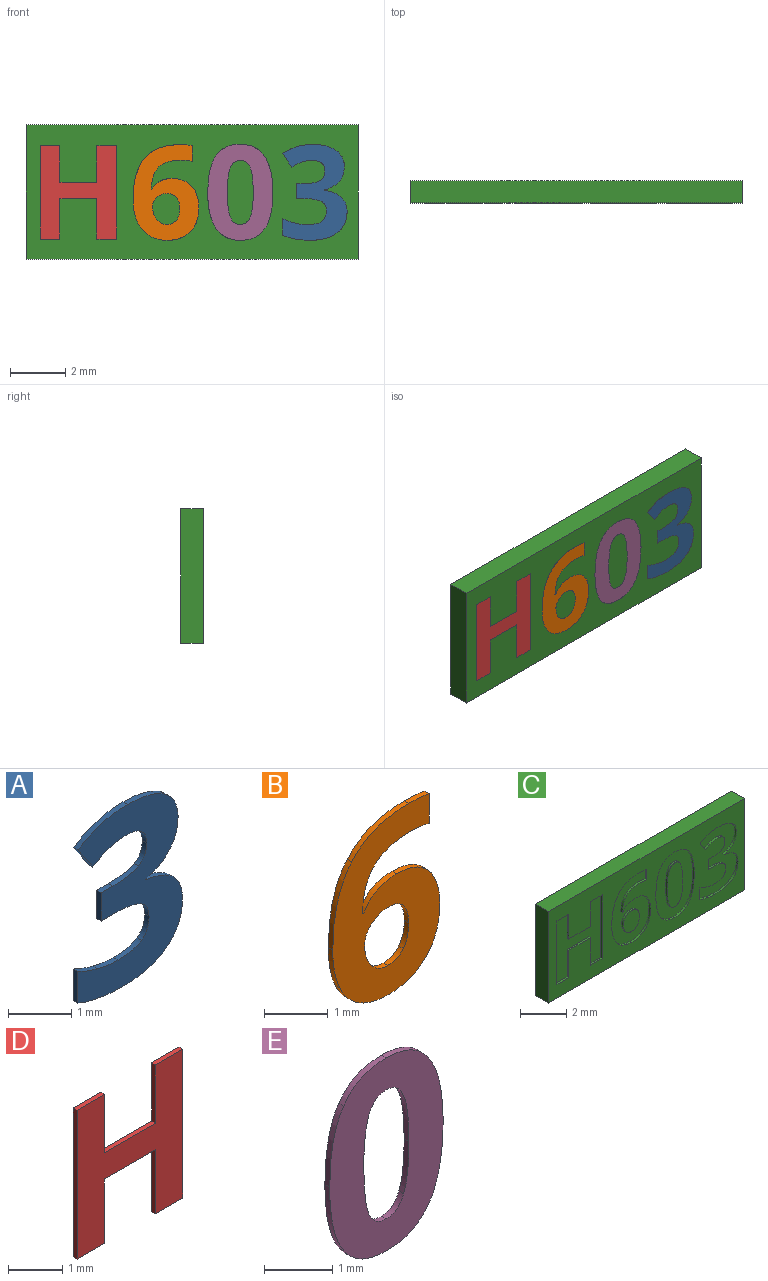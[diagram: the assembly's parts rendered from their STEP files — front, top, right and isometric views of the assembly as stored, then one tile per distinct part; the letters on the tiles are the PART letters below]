
ASSEMBLY  parts=5 mates=4
PART A: 29 faces, bbox 2.3x0.1x3.5 mm
  f0: plane 3.47x2.33mm, normal (0,-1,0), area 4.3mm2, adj f1,f2,f3,f4,f5,f6,f7,f8
  f1: extruded ~0.83x0.21mm, area 0.1mm2, adj f0,f2,f25,f27
  f2: extruded ~1.1x0.33mm, area 0.1mm2, adj f0,f1,f3,f25
  f3: plane 0.49x0.33mm, normal (-0.83,0,-0.56), area 0.1mm2, adj f0,f2,f4,f25
  f4: extruded ~0.38x0.19mm, area 0mm2, adj f0,f3,f5,f25
  f5: extruded ~0.34x0.1mm, area 0mm2, adj f0,f4,f6,f25
  f6: extruded ~0.48x0.38mm, area 0.1mm2, adj f0,f5,f7,f25
  f7: extruded ~0.35x0.18mm, area 0mm2, adj f0,f6,f8,f25
  f8: extruded ~0.57x0.1mm, area 0.1mm2, adj f0,f7,f9,f25
  f9: plane 0.26x0.1mm, normal (0,0,1), area 0mm2, adj f0,f8,f10,f25
  f10: plane 0.55x0.1mm, normal (-1,0,0), area 0.1mm2, adj f0,f9,f11,f25
  f11: plane 0.26x0.1mm, normal (0,0,-1), area 0mm2, adj f0,f10,f12,f25
  f12: extruded ~0.62x0.1mm, area 0.1mm2, adj f0,f11,f13,f25
  f13: extruded ~0.34x0.19mm, area 0mm2, adj f0,f12,f14,f25
  f14: extruded ~0.39x0.17mm, area 0mm2, adj f0,f13,f15,f25
  f15: extruded ~0.52x0.12mm, area 0.1mm2, adj f0,f14,f16,f25
  f16: extruded ~0.47x0.1mm, area 0mm2, adj f0,f15,f17,f25
  f17: extruded ~0.43x0.16mm, area 0mm2, adj f0,f16,f18,f25
  f18: plane 0.61x0.1mm, normal (-1,0,0), area 0.1mm2, adj f0,f17,f19,f25
  f19: extruded ~0.97x0.18mm, area 0.1mm2, adj f0,f18,f20,f25
  f20: extruded ~1.01x0.27mm, area 0.1mm2, adj f0,f19,f21,f25
  f21: extruded ~0.76x0.35mm, area 0.1mm2, adj f0,f20,f22,f25
  f22: extruded ~0.53x0.21mm, area 0.1mm2, adj f0,f21,f23,f25
  f23: extruded ~0.62x0.25mm, area 0.1mm2, adj f0,f22,f24,f25
  f24: plane 0.1x0.01mm, normal (1,0,0), area 0mm2, adj f0,f23,f25,f26
  f25: plane 3.47x2.33mm, normal (0,1,0), area 4.3mm2, adj f1,f2,f3,f4,f5,f6,f7,f8
  f26: extruded ~0.54x0.3mm, area 0.1mm2, adj f0,f24,f25,f28
  f27: extruded ~0.59x0.3mm, area 0.1mm2, adj f0,f1,f25,f28
  f28: extruded ~0.54x0.19mm, area 0.1mm2, adj f0,f25,f26,f27
PART B: 27 faces, bbox 2.4x0.1x3.5 mm
  f0: plane 3.46x2.38mm, normal (0,-1,0), area 4.8mm2, adj f1,f2,f3,f4,f5,f6,f7,f8
  f1: extruded ~0.51x0.43mm, area 0.1mm2, adj f0,f2,f20,f22
  f2: extruded ~0.65x0.17mm, area 0.1mm2, adj f0,f1,f3,f20
  f3: extruded ~0.84x0.32mm, area 0.1mm2, adj f0,f2,f4,f20
  f4: extruded ~0.85x0.3mm, area 0.1mm2, adj f0,f3,f5,f20
  f5: extruded ~0.78x0.26mm, area 0.1mm2, adj f0,f4,f6,f20
  f6: extruded ~0.71x0.28mm, area 0.1mm2, adj f0,f5,f7,f20
  f7: extruded ~0.73x0.39mm, area 0.1mm2, adj f0,f6,f8,f20
  f8: plane 0.1x0.03mm, normal (0,0,1), area 0mm2, adj f0,f7,f9,f20
  f9: extruded ~0.62x0.14mm, area 0.1mm2, adj f0,f8,f10,f20
  f10: extruded ~0.35x0.33mm, area 0mm2, adj f0,f9,f11,f20
  f11: extruded ~0.6x0.11mm, area 0.1mm2, adj f0,f10,f12,f20
  f12: extruded ~0.41x0.1mm, area 0mm2, adj f0,f11,f13,f20
  f13: plane 0.57x0.1mm, normal (1,0,0), area 0.1mm2, adj f0,f12,f14,f20
  f14: extruded ~0.45x0.1mm, area 0mm2, adj f0,f13,f20,f21
  f15: extruded ~0.46x0.14mm, area 0mm2, adj f0,f16,f20,f25
  f16: extruded ~0.33x0.15mm, area 0mm2, adj f0,f15,f17,f20
  f17: extruded ~0.37x0.14mm, area 0mm2, adj f0,f16,f18,f20
  f18: extruded ~0.34x0.14mm, area 0mm2, adj f0,f17,f19,f20
  f19: extruded ~0.39x0.11mm, area 0mm2, adj f0,f18,f20,f24
  f20: plane 3.46x2.38mm, normal (0,1,0), area 4.8mm2, adj f1,f2,f3,f4,f5,f6,f7,f8
  f21: extruded ~1.27x0.49mm, area 0.1mm2, adj f0,f14,f20,f23
  f22: extruded ~0.8x0.15mm, area 0.1mm2, adj f0,f1,f20,f23
  f23: extruded ~1.49x0.42mm, area 0.2mm2, adj f0,f20,f21,f22
  f24: extruded ~0.44x0.12mm, area 0mm2, adj f0,f19,f20,f26
  f25: extruded ~0.37x0.19mm, area 0mm2, adj f0,f15,f20,f26
  f26: extruded ~0.35x0.15mm, area 0mm2, adj f0,f20,f24,f25
PART C: 92 faces, bbox 12x0.8x4.9 mm
  f0: plane 12x4.85mm, normal (0,-1,0), area 35.7mm2, adj f1,f2,f3,f4,f6,f7,f8,f9
  f1: plane 12x0.8mm, normal (0,0,-1), area 9.6mm2, adj f0,f2,f4,f5
  f2: plane 4.85x0.8mm, normal (1,0,0), area 3.9mm2, adj f0,f1,f3,f5
  f3: plane 12x0.8mm, normal (0,0,1), area 9.6mm2, adj f0,f2,f4,f5
  f4: plane 4.85x0.8mm, normal (-1,0,0), area 3.9mm2, adj f0,f1,f3,f5
  f5: plane 12x4.85mm, normal (0,1,0), area 58.2mm2, adj f1,f2,f3,f4
  f6: extruded ~0.59x0.3mm, area 0.1mm2, adj f0,f7,f32,f33
  f7: extruded ~0.83x0.21mm, area 0.1mm2, adj f0,f6,f8,f33
  f8: extruded ~1.1x0.33mm, area 0.1mm2, adj f0,f7,f9,f33
  f9: plane 0.49x0.33mm, normal (0.83,0,0.56), area 0.1mm2, adj f0,f8,f10,f33
  f10: extruded ~0.38x0.19mm, area 0mm2, adj f0,f9,f11,f33
  f11: extruded ~0.34x0.1mm, area 0mm2, adj f0,f10,f12,f33
  f12: extruded ~0.48x0.38mm, area 0.1mm2, adj f0,f11,f13,f33
  f13: extruded ~0.35x0.18mm, area 0mm2, adj f0,f12,f14,f33
  f14: extruded ~0.57x0.1mm, area 0.1mm2, adj f0,f13,f15,f33
  f15: plane 0.26x0.1mm, normal (0,0,-1), area 0mm2, adj f0,f14,f16,f33
  f16: plane 0.55x0.1mm, normal (1,0,0), area 0.1mm2, adj f0,f15,f17,f33
  f17: plane 0.26x0.1mm, normal (0,0,1), area 0mm2, adj f0,f16,f18,f33
  f18: extruded ~0.62x0.1mm, area 0.1mm2, adj f0,f17,f19,f33
  f19: extruded ~0.34x0.19mm, area 0mm2, adj f0,f18,f20,f33
  f20: extruded ~0.39x0.17mm, area 0mm2, adj f0,f19,f21,f33
  f21: extruded ~0.52x0.12mm, area 0.1mm2, adj f0,f20,f22,f33
  f22: extruded ~0.47x0.1mm, area 0mm2, adj f0,f21,f23,f33
  f23: extruded ~0.43x0.16mm, area 0mm2, adj f0,f22,f24,f33
  f24: plane 0.61x0.1mm, normal (1,0,0), area 0.1mm2, adj f0,f23,f25,f33
  f25: extruded ~0.97x0.18mm, area 0.1mm2, adj f0,f24,f26,f33
  f26: extruded ~1.01x0.27mm, area 0.1mm2, adj f0,f25,f27,f33
  f27: extruded ~0.76x0.35mm, area 0.1mm2, adj f0,f26,f28,f33
  f28: extruded ~0.53x0.21mm, area 0.1mm2, adj f0,f27,f29,f33
  f29: extruded ~0.62x0.25mm, area 0.1mm2, adj f0,f28,f30,f33
  f30: plane 0.1x0.01mm, normal (-1,0,0), area 0mm2, adj f0,f29,f31,f33
  f31: extruded ~0.54x0.3mm, area 0.1mm2, adj f0,f30,f32,f33
  f32: extruded ~0.54x0.19mm, area 0.1mm2, adj f0,f6,f31,f33
  f33: plane 3.47x2.33mm, normal (0,-1,0), area 4.3mm2, adj f6,f7,f8,f9,f10,f11,f12,f13
  f34: extruded ~0.8x0.15mm, area 0.1mm2, adj f0,f35,f58,f59
  f35: extruded ~0.51x0.43mm, area 0.1mm2, adj f0,f34,f36,f59
  f36: extruded ~0.65x0.17mm, area 0.1mm2, adj f0,f35,f37,f59
  f37: extruded ~0.84x0.32mm, area 0.1mm2, adj f0,f36,f38,f59
  f38: extruded ~0.85x0.3mm, area 0.1mm2, adj f0,f37,f39,f59
  f39: extruded ~0.78x0.26mm, area 0.1mm2, adj f0,f38,f40,f59
  f40: extruded ~0.71x0.28mm, area 0.1mm2, adj f0,f39,f41,f59
  f41: extruded ~0.73x0.39mm, area 0.1mm2, adj f0,f40,f42,f59
  f42: plane 0.1x0.03mm, normal (0,0,-1), area 0mm2, adj f0,f41,f43,f59
  f43: extruded ~0.62x0.14mm, area 0.1mm2, adj f0,f42,f44,f59
  f44: extruded ~0.35x0.33mm, area 0mm2, adj f0,f43,f45,f59
  f45: extruded ~0.6x0.11mm, area 0.1mm2, adj f0,f44,f46,f59
  f46: extruded ~0.41x0.1mm, area 0mm2, adj f0,f45,f47,f59
  f47: plane 0.57x0.1mm, normal (-1,0,0), area 0.1mm2, adj f0,f46,f48,f59
  f48: extruded ~0.45x0.1mm, area 0mm2, adj f0,f47,f49,f59
  f49: extruded ~1.27x0.49mm, area 0.1mm2, adj f0,f48,f58,f59
  f50: extruded ~0.37x0.19mm, area 0mm2, adj f51,f57,f59,f60
  f51: extruded ~0.46x0.14mm, area 0mm2, adj f50,f52,f59,f60
  f52: extruded ~0.33x0.15mm, area 0mm2, adj f51,f53,f59,f60
  f53: extruded ~0.37x0.14mm, area 0mm2, adj f52,f54,f59,f60
  f54: extruded ~0.34x0.14mm, area 0mm2, adj f53,f55,f59,f60
  f55: extruded ~0.39x0.11mm, area 0mm2, adj f54,f56,f59,f60
  f56: extruded ~0.44x0.12mm, area 0mm2, adj f55,f57,f59,f60
  f57: extruded ~0.35x0.15mm, area 0mm2, adj f50,f56,f59,f60
  f58: extruded ~1.49x0.42mm, area 0.2mm2, adj f0,f34,f49,f59
  f59: plane 3.46x2.38mm, normal (0,-1,0), area 4.8mm2, adj f34,f35,f36,f37,f38,f39,f40,f41
  f60: plane 1.12x0.98mm, normal (0,-1,0), area 0.9mm2, adj f50,f51,f52,f53,f54,f55,f56,f57
  f61: extruded ~1.3x0.3mm, area 0.1mm2, adj f0,f62,f76,f77
  f62: extruded ~0.88x0.44mm, area 0.1mm2, adj f0,f61,f63,f77
  f63: extruded ~0.89x0.42mm, area 0.1mm2, adj f0,f62,f64,f77
  f64: extruded ~1.32x0.29mm, area 0.1mm2, adj f0,f63,f65,f77
  f65: extruded ~1.29x0.3mm, area 0.1mm2, adj f0,f64,f66,f77
  f66: extruded ~0.88x0.44mm, area 0.1mm2, adj f0,f65,f67,f77
  f67: extruded ~0.89x0.42mm, area 0.1mm2, adj f0,f66,f76,f77
  f68: extruded ~0.89x0.11mm, area 0.1mm2, adj f69,f75,f77,f78
  f69: extruded ~0.36x0.27mm, area 0mm2, adj f68,f70,f77,f78
  f70: extruded ~0.36x0.27mm, area 0mm2, adj f69,f71,f77,f78
  f71: extruded ~0.89x0.11mm, area 0.1mm2, adj f70,f72,f77,f78
  f72: extruded ~0.89x0.11mm, area 0.1mm2, adj f71,f73,f77,f78
  f73: extruded ~0.36x0.27mm, area 0mm2, adj f72,f74,f77,f78
  f74: extruded ~0.36x0.27mm, area 0mm2, adj f73,f75,f77,f78
  f75: extruded ~0.89x0.11mm, area 0.1mm2, adj f68,f74,f77,f78
  f76: extruded ~1.31x0.29mm, area 0.1mm2, adj f0,f61,f67,f77
  f77: plane 3.47x2.36mm, normal (0,-1,0), area 5mm2, adj f61,f62,f63,f64,f65,f66,f67,f68
  f78: plane 2.32x0.94mm, normal (0,-1,0), area 1.8mm2, adj f68,f69,f70,f71,f72,f73,f74,f75
  f79: plane 3.37x0.1mm, normal (-1,0,0), area 0.3mm2, adj f0,f80,f90,f91
  f80: plane 0.71x0.1mm, normal (0,0,-1), area 0.1mm2, adj f0,f79,f81,f91
  f81: plane 1.32x0.1mm, normal (1,0,0), area 0.1mm2, adj f0,f80,f82,f91
  f82: plane 1.33x0.1mm, normal (0,0,-1), area 0.1mm2, adj f0,f81,f83,f91
  f83: plane 1.32x0.1mm, normal (-1,0,0), area 0.1mm2, adj f0,f82,f84,f91
  f84: plane 0.72x0.1mm, normal (0,0,-1), area 0.1mm2, adj f0,f83,f85,f91
  f85: plane 3.37x0.1mm, normal (1,0,0), area 0.3mm2, adj f0,f84,f86,f91
  f86: plane 0.72x0.1mm, normal (0,0,1), area 0.1mm2, adj f0,f85,f87,f91
  f87: plane 1.46x0.1mm, normal (-1,0,0), area 0.1mm2, adj f0,f86,f88,f91
  f88: plane 1.33x0.1mm, normal (0,0,1), area 0.1mm2, adj f0,f87,f89,f91
  f89: plane 1.46x0.1mm, normal (1,0,0), area 0.1mm2, adj f0,f88,f90,f91
  f90: plane 0.71x0.1mm, normal (0,0,1), area 0.1mm2, adj f0,f79,f89,f91
  f91: plane 3.37x2.76mm, normal (0,-1,0), area 5.6mm2, adj f79,f80,f81,f82,f83,f84,f85,f86
PART D: 14 faces, bbox 2.8x0.1x3.4 mm
  f0: plane 3.37x2.76mm, normal (0,-1,0), area 5.6mm2, adj f1,f2,f3,f4,f5,f6,f7,f8
  f1: plane 0.71x0.1mm, normal (0,0,1), area 0.1mm2, adj f0,f2,f10,f12
  f2: plane 1.32x0.1mm, normal (-1,0,0), area 0.1mm2, adj f0,f1,f3,f10
  f3: plane 1.33x0.1mm, normal (0,0,1), area 0.1mm2, adj f0,f2,f4,f10
  f4: plane 1.32x0.1mm, normal (1,0,0), area 0.1mm2, adj f0,f3,f5,f10
  f5: plane 0.72x0.1mm, normal (0,0,1), area 0.1mm2, adj f0,f4,f6,f10
  f6: plane 3.37x0.1mm, normal (-1,0,0), area 0.3mm2, adj f0,f5,f7,f10
  f7: plane 0.72x0.1mm, normal (0,0,-1), area 0.1mm2, adj f0,f6,f8,f10
  f8: plane 1.46x0.1mm, normal (1,0,0), area 0.1mm2, adj f0,f7,f9,f10
  f9: plane 1.33x0.1mm, normal (0,0,-1), area 0.1mm2, adj f0,f8,f10,f11
  f10: plane 3.37x2.76mm, normal (0,1,0), area 5.6mm2, adj f1,f2,f3,f4,f5,f6,f7,f8
  f11: plane 1.46x0.1mm, normal (-1,0,0), area 0.1mm2, adj f0,f9,f10,f13
  f12: plane 3.37x0.1mm, normal (1,0,0), area 0.3mm2, adj f0,f1,f10,f13
  f13: plane 0.71x0.1mm, normal (0,0,-1), area 0.1mm2, adj f0,f10,f11,f12
PART E: 18 faces, bbox 2.4x0.1x3.5 mm
  f0: plane 3.47x2.36mm, normal (0,-1,0), area 5mm2, adj f1,f2,f3,f4,f5,f6,f7,f8
  f1: extruded ~0.88x0.44mm, area 0.1mm2, adj f0,f2,f11,f13
  f2: extruded ~0.89x0.42mm, area 0.1mm2, adj f0,f1,f3,f11
  f3: extruded ~1.32x0.29mm, area 0.1mm2, adj f0,f2,f4,f11
  f4: extruded ~1.29x0.3mm, area 0.1mm2, adj f0,f3,f5,f11
  f5: extruded ~0.88x0.44mm, area 0.1mm2, adj f0,f4,f11,f12
  f6: extruded ~0.36x0.27mm, area 0mm2, adj f0,f7,f11,f16
  f7: extruded ~0.36x0.27mm, area 0mm2, adj f0,f6,f8,f11
  f8: extruded ~0.89x0.11mm, area 0.1mm2, adj f0,f7,f9,f11
  f9: extruded ~0.89x0.11mm, area 0.1mm2, adj f0,f8,f10,f11
  f10: extruded ~0.36x0.27mm, area 0mm2, adj f0,f9,f11,f15
  f11: plane 3.47x2.36mm, normal (0,1,0), area 5mm2, adj f1,f2,f3,f4,f5,f6,f7,f8
  f12: extruded ~0.89x0.42mm, area 0.1mm2, adj f0,f5,f11,f14
  f13: extruded ~1.3x0.3mm, area 0.1mm2, adj f0,f1,f11,f14
  f14: extruded ~1.31x0.29mm, area 0.1mm2, adj f0,f11,f12,f13
  f15: extruded ~0.36x0.27mm, area 0mm2, adj f0,f10,f11,f17
  f16: extruded ~0.89x0.11mm, area 0.1mm2, adj f0,f6,f11,f17
  f17: extruded ~0.89x0.11mm, area 0.1mm2, adj f0,f11,f15,f16
PLACE A t=(2.92,0.38,-0.02)mm
PLACE B t=(-2.46,0.38,-0.02)mm
PLACE C t=(-0.02,0.38,-0.02)mm
PLACE D t=(-0.02,0.38,-0.02)mm
PLACE E t=(-1.12,0.38,-0.02)mm
MATE fastened B.f0 <-> C.f0  axis (0,-1,0) through (-0.01,-0.42,1.09)mm
MATE fastened D.f0 <-> C.f0  axis (0,-1,0) through (-5.5,-0.42,-1.72)mm
MATE fastened E.f0 <-> C.f78  axis (0,-1,0) through (1.73,-0.42,-1.19)mm
MATE fastened A.f0 <-> C.f0  axis (0,-1,0) through (3.26,-0.42,-1.58)mm
